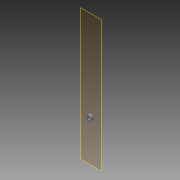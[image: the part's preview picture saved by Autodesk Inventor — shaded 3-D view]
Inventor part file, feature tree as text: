
AUTODESK INVENTOR PART (.ipt)
format: ipt  version: 2015 (Build 190159000, 159)  size: 68,608 bytes
history: native  units: in
note: dims shown in document units (in); Inventor stores cm internally (conversion verified against a paired STEP export)
features: plane x2, sketch x1, extrude x1, reference x1
ambient origin geometry x8: Origin, YZ Plane, XZ Plane, XY Plane, X Axis, Y Axis, Z Axis, Center Point
bodies: Solid1 (feature_tree)
feature tree (5):
  plane  "Work Plane1"
  sketch  "Sketch1"  dims[d0=1.0in d1=0.0in]
  plane  "Work Plane2"
  extrude  "Extrusion1"  [1 undecoded]
  reference  "Reference1"
note: 1 required parameter value undecoded (feature->parameter linkage not recoverable at this tier; creation-order binding heuristic only, values carry confidence <= 0.55)
